# Revit family: Single With Trim
name_source: partatom
category: Doors
revit_build: Autodesk Revit Architecture 2012 (Build: 20110309_2315(x64)
units: mm (PartAtom-declared; Revit-internal decimal feet)

## types (5) — shared parameters
Door = <By Category>
DoorSwingAngle = 90.00°
Doorknob = <By Category>
Frame Projection Ext. = 0' - 1"
Frame Projection Int. = 0' - 1"
Frame Width = 0' - 3"
FrameThickness = 0' - 0 1/2"
FrameThicknessTop = 0' - 0 1/2"
Function = Interior
Height = 6' - 8"
Leaf = <By Category>
Rough Height = 6' - 8 1/2"
Trim = <By Category>
Wall Closure = By host

## per-type parameters (varying)
| type | DoorknobHeightO.C. | DoorknobSideDistO.C. | Rough Width | Width |
| 32" x 80" | 3' - 4" | 0' - 2 1/2" | 2' - 9" | 2' - 8" |
| 36" x 80" | 3' - 4 1/32" | 0' - 2 13/32" | 3' - 1" | 3' - 0" |
| 28" x 80" | 3' - 4" | 0' - 2 1/2" | 2' - 5" | 2' - 4" |
| 24" x 80" | 3' - 4" | 0' - 2 1/2" | 2' - 1" | 2' - 0" |
| 30" x 80 | 3' - 4" | 0' - 2 1/2" | 2' - 7" | 2' - 6" |

## geometry (parser evidence)
native form markers: Sweep x3
no freeform markers — native parametric forms only
